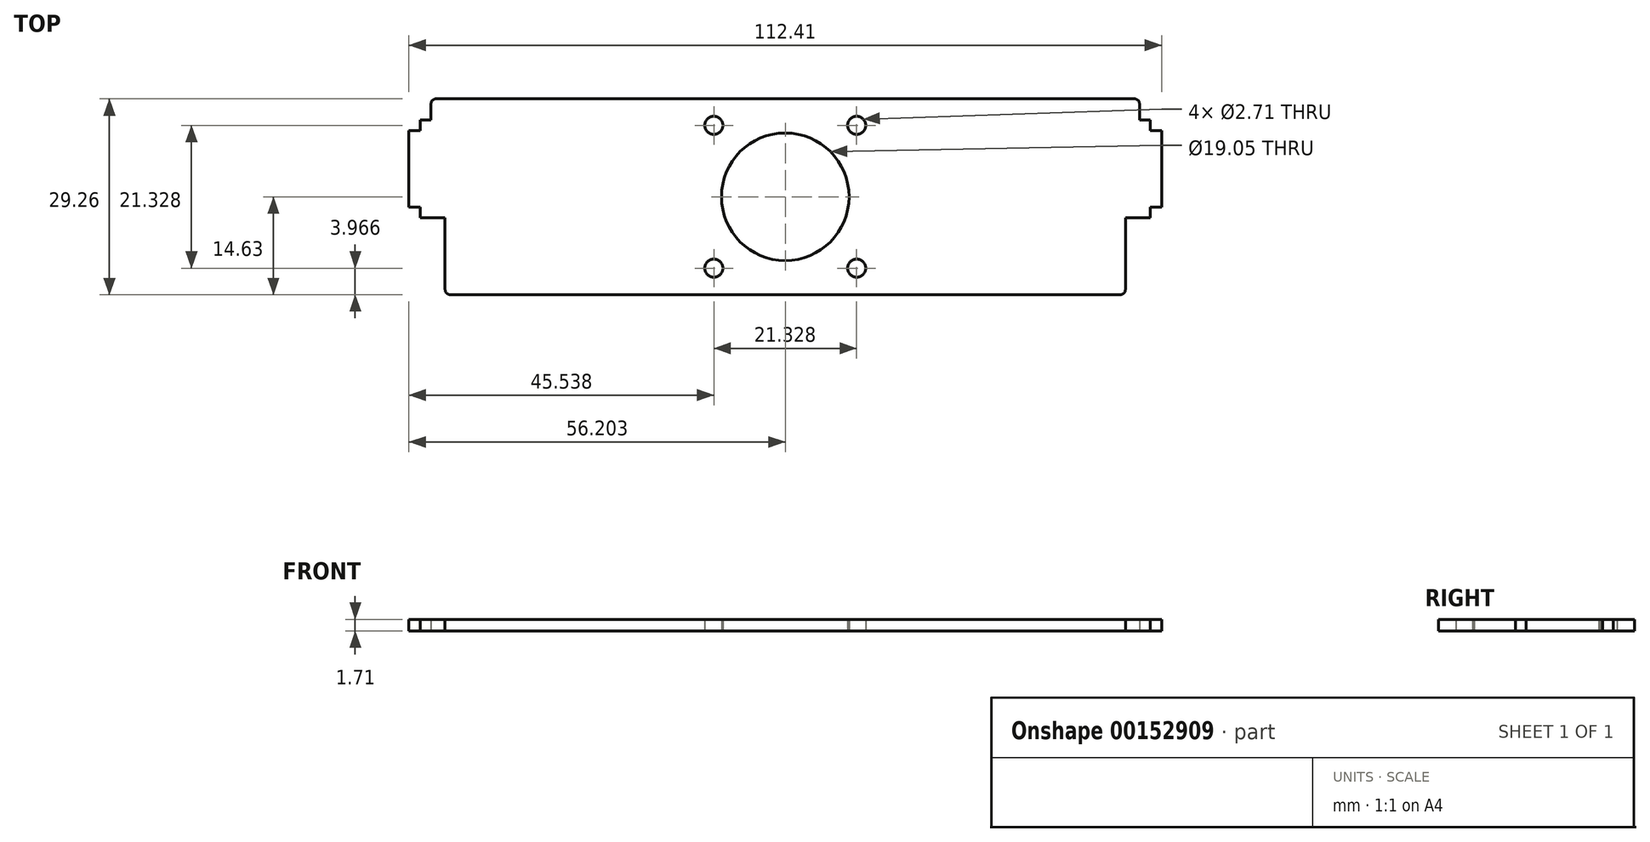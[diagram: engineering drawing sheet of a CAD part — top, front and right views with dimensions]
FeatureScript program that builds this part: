
annotation { "Feature Type Name" : "Feature", "Feature Type Description" : "" }
export const myFeature = defineFeature(function(context is Context, id is Id, definition is map)
    precondition{}
    {
        {
            var Q0;
            Q0=qCreatedBy(makeId("Top.planeOp"),FACE);
            var sketch = newSketch(context, id + "F0", { "sketchPlane" : qUnion([Q0])});
            skLineSegment(sketch, "E0.bottom", {"start": v(0, 0) * mm, "end": v(1.7, 0) * mm});
            skLineSegment(sketch, "E0.top", {"start": v(0, -11.4) * mm, "end": v(1.7, -11.4) * mm});
            skLineSegment(sketch, "E0.left", {"start": v(0, 0) * mm, "end": v(0, -11.4) * mm});
            skLineSegment(sketch, "E0.right", {"start": v(1.7, 0) * mm, "end": v(1.7, -11.4) * mm, "construction": true});
            skLineSegment(sketch, "E1", {"start": v(1.7, 0) * mm, "end": v(1.7, 1.59) * mm});
            skLineSegment(sketch, "E2", {"start": v(1.7, 1.59) * mm, "end": v(3.3, 1.59) * mm});
            skLineSegment(sketch, "E3", {"start": v(3.3, 1.59) * mm, "end": v(3.3, 4.76) * mm});
            skLineSegment(sketch, "E4", {"start": v(1.7, -11.4) * mm, "end": v(1.7, -13) * mm});
            skLineSegment(sketch, "E5", {"start": v(1.7, -13) * mm, "end": v(5.4, -13) * mm});
            skLineSegment(sketch, "E6", {"start": v(5.4, -13) * mm, "end": v(5.4, -24.5) * mm});
            skLineSegment(sketch, "E7", {"start": v(3.3, 4.76) * mm, "end": v(109.1, 4.76) * mm});
            skLineSegment(sketch, "E8", {"start": v(109.1, 4.76) * mm, "end": v(109.1, 1.59) * mm});
            skLineSegment(sketch, "E9", {"start": v(109.1, 1.59) * mm, "end": v(110.7, 1.59) * mm});
            skLineSegment(sketch, "E10", {"start": v(110.7, 1.59) * mm, "end": v(110.7, 0) * mm});
            skLineSegment(sketch, "E11.bottom", {"start": v(110.7, 0) * mm, "end": v(112.4, 0) * mm});
            skLineSegment(sketch, "E11.top", {"start": v(110.7, -11.4) * mm, "end": v(112.4, -11.4) * mm});
            skLineSegment(sketch, "E11.left", {"start": v(110.7, 0) * mm, "end": v(110.7, -11.4) * mm, "construction": true});
            skLineSegment(sketch, "E11.right", {"start": v(112.4, 0) * mm, "end": v(112.4, -11.4) * mm});
            skLineSegment(sketch, "E12", {"start": v(110.7, -11.4) * mm, "end": v(110.7, -13) * mm});
            skLineSegment(sketch, "E13", {"start": v(110.7, -13) * mm, "end": v(107, -13) * mm});
            skLineSegment(sketch, "E14", {"start": v(107, -13) * mm, "end": v(107, -24.5) * mm});
            skLineSegment(sketch, "E15", {"start": v(5.4, -24.5) * mm, "end": v(107, -24.5) * mm});
            skLineSegment(sketch, "E16.bottom", {"start": v(66.87, 0.8) * mm, "end": v(45.54, 0.8) * mm, "construction": true});
            skLineSegment(sketch, "E16.top", {"start": v(66.87, -20.53) * mm, "end": v(45.54, -20.53) * mm, "construction": true});
            skLineSegment(sketch, "E16.left", {"start": v(66.87, 0.8) * mm, "end": v(66.87, -20.53) * mm, "construction": true});
            skLineSegment(sketch, "E16.right", {"start": v(45.54, 0.8) * mm, "end": v(45.54, -20.53) * mm, "construction": true});
            skPoint(sketch, "E16.middle", {"position": v(56.2, -9.87) * mm});
            skCircle(sketch, "E17", {"center": v(56.2, -9.87) * mm, "radius": 9.53 * mm});
            skLineSegment(sketch, "E18", {"start": v(56.2, -20.53) * mm, "end": v(56.2, -24.5) * mm, "construction": true});
            skLineSegment(sketch, "E19", {"start": v(56.2, 0.8) * mm, "end": v(56.2, 4.76) * mm, "construction": true});
            skCircle(sketch, "E20", {"center": v(45.54, 0.8) * mm, "radius": 1.35 * mm});
            skCircle(sketch, "E21", {"center": v(45.54, -20.53) * mm, "radius": 1.35 * mm});
            skCircle(sketch, "E22", {"center": v(66.87, -20.53) * mm, "radius": 1.35 * mm});
            skCircle(sketch, "E23", {"center": v(66.87, 0.8) * mm, "radius": 1.35 * mm});
            skSolve(sketch);
        }
        {
            var Q0;
            Q0 = qSketchRegion(id + "F0", true);
            extrude(context, id + "F1", {"entities" : qUnion([Q0]), "depth" : 1.7 * mm});
        }
        {
            var Q0;
            Q0=makeQuery(id+"F1.opExtrude","SWEPT_EDGE",EDGE,{"disambiguationData":[OSD([sQuery(id+"F0.wireOp",EDGE,"E3"),sQuery(id+"F0.wireOp",EDGE,"E7")])]});
            var Q1;
            Q1=makeQuery(id+"F1.opExtrude","SWEPT_EDGE",EDGE,{"disambiguationData":[OSD([sQuery(id+"F0.wireOp",EDGE,"E6"),sQuery(id+"F0.wireOp",EDGE,"E15")])]});
            var Q2;
            Q2=makeQuery(id+"F1.opExtrude","SWEPT_EDGE",EDGE,{"disambiguationData":[OSD([sQuery(id+"F0.wireOp",EDGE,"E14"),sQuery(id+"F0.wireOp",EDGE,"E15")])]});
            var Q3;
            Q3=makeQuery(id+"F1.opExtrude","SWEPT_EDGE",EDGE,{"disambiguationData":[OSD([sQuery(id+"F0.wireOp",EDGE,"E7"),sQuery(id+"F0.wireOp",EDGE,"E8")])]});
            fillet(context, id + "F2", {"entities" : qUnion([Q0, Q1, Q2, Q3]), "radius" : 0.76 * mm, "tangentPropagation" : true, "allowEdgeOverflow" : false});
        }
    });
